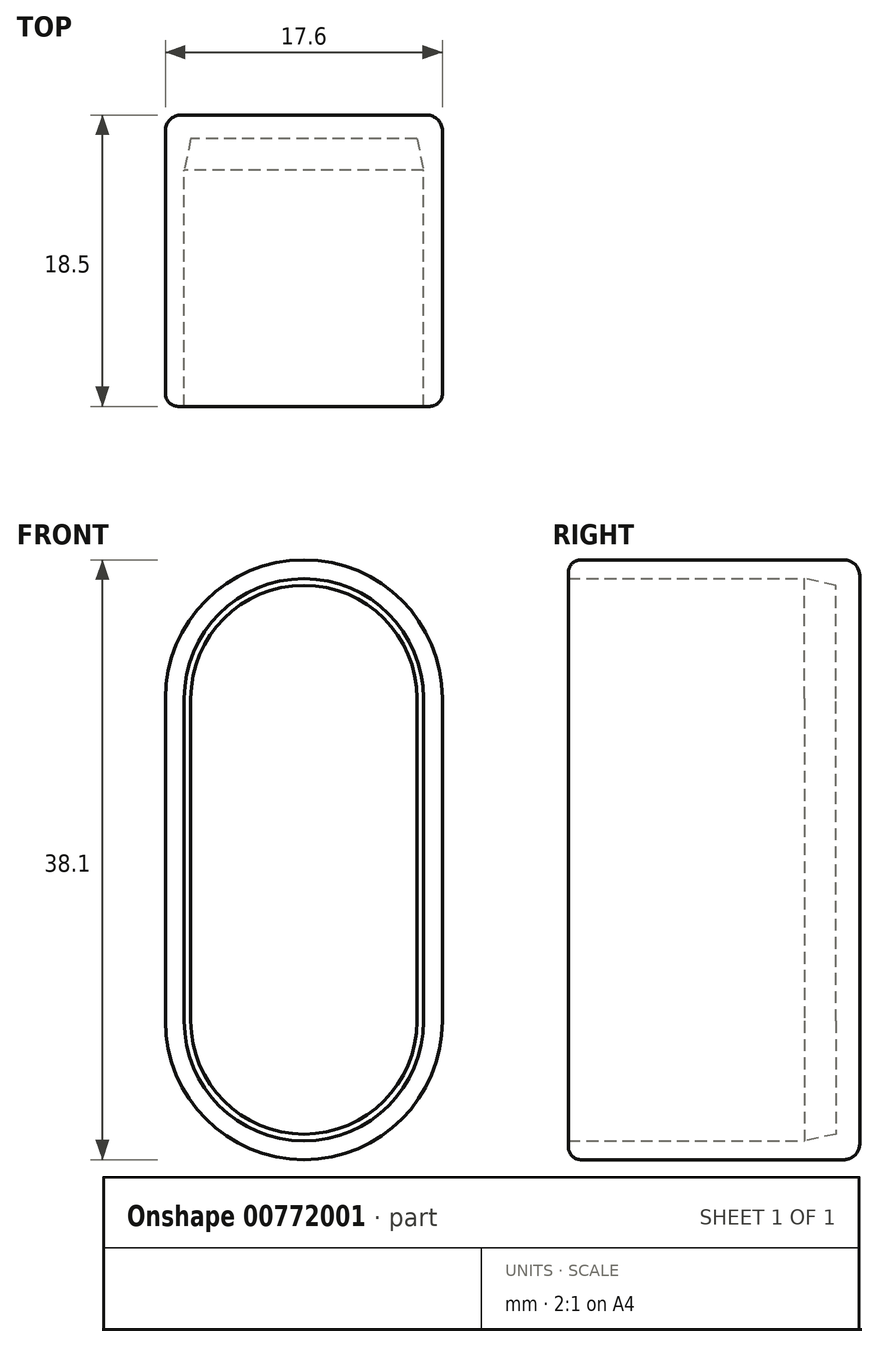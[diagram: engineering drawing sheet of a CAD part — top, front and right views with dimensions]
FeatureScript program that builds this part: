
annotation { "Feature Type Name" : "Feature", "Feature Type Description" : "" }
export const myFeature = defineFeature(function(context is Context, id is Id, definition is map)
    precondition{}
    {
        {
            var Q0;
            Q0=qCreatedBy(makeId("Front.planeOp"),FACE);
            var sketch = newSketch(context, id + "F0", { "sketchPlane" : qUnion([Q0])});
            skLineSegment(sketch, "E0", {"start": v(0, 0) * mm, "end": v(0, 20.5) * mm, "construction": true});
            skArc(sketch, "E1", {"start": v(7.6, 20.5) * mm, "mid": v(0, 28.1) * mm, "end": v(-7.6, 20.5) * mm});
            skArc(sketch, "E2", {"start": v(-7.6, 0) * mm, "mid": v(0, -7.6) * mm, "end": v(7.6, 0) * mm});
            skLineSegment(sketch, "E3", {"start": v(-7.6, 20.5) * mm, "end": v(-7.6, 0) * mm});
            skLineSegment(sketch, "E4", {"start": v(7.6, 20.5) * mm, "end": v(7.6, 0) * mm});
            skArc(sketch, "E5.0", {"start": v(8.8, 20.5) * mm, "mid": v(0, 29.3) * mm, "end": v(-8.8, 20.5) * mm});
            skLineSegment(sketch, "E5.1", {"start": v(8.8, 20.5) * mm, "end": v(8.8, 0) * mm});
            skArc(sketch, "E5.2", {"start": v(-8.8, 0) * mm, "mid": v(0, -8.8) * mm, "end": v(8.8, 0) * mm});
            skLineSegment(sketch, "E5.3", {"start": v(-8.8, 20.5) * mm, "end": v(-8.8, 0) * mm});
            skSolve(sketch);
        }
        {
            var Q0;
            Q0=makeQuery(id+"F0.imprint","IMPRINT",FACE,{"disambiguationData":[TD([[makeQuery(id+"F0.imprint","IMPRINT",EDGE,{"derivedFrom":sQuery(id+"F0.wireOp",EDGE,"E1")}),-1.0]])]});
            extrude(context, id + "F1", {"entities" : qUnion([Q0]), "depth" : 15 * mm, "offsetDistance" : 25 * mm});
        }
        {
            var Q0;
            Q0=makeQuery(id+"F1.opExtrude","CAP_FACE",FACE,{"disambiguationData":[OSD([sQuery(id+"F0.wireOp",EDGE,"E1"),sQuery(id+"F0.wireOp",EDGE,"E2"),sQuery(id+"F0.wireOp",EDGE,"E3"),sQuery(id+"F0.wireOp",EDGE,"E4"),sQuery(id+"F0.wireOp",EDGE,"E5.0"),sQuery(id+"F0.wireOp",EDGE,"E5.1"),sQuery(id+"F0.wireOp",EDGE,"E5.2"),sQuery(id+"F0.wireOp",EDGE,"E5.3")])],"isStart":true});
            cPlane(context, id + "F2", {"entities" : qUnion([Q0]), "cplaneType" : CPlaneType.OFFSET, "offset" : 2.4 * mm, "width" : 150 * mm, "height" : 150 * mm});
        }
        {
            var Q0;
            Q0=qCreatedBy(id+"F2.planeOp",FACE);
            var sketch = newSketch(context, id + "F3", { "sketchPlane" : qUnion([Q0])});
            skLineSegment(sketch, "E6.0", {"start": v(-7.1, 20.5) * mm, "end": v(-7.1, 0) * mm});
            skArc(sketch, "E6.1", {"start": v(-7.1, 20.5) * mm, "mid": v(0, 27.6) * mm, "end": v(7.1, 20.5) * mm});
            skLineSegment(sketch, "E6.2", {"start": v(7.1, 20.5) * mm, "end": v(7.1, 0) * mm});
            skArc(sketch, "E6.3", {"start": v(7.1, 0) * mm, "mid": v(0, -7.1) * mm, "end": v(-7.1, 0) * mm});
            skSolve(sketch);
        }
        {
            var Q0;
            Q0=makeQuery(id+"F1.opExtrude","CAP_FACE",FACE,{"disambiguationData":[OSD([sQuery(id+"F0.wireOp",EDGE,"E1"),sQuery(id+"F0.wireOp",EDGE,"E2"),sQuery(id+"F0.wireOp",EDGE,"E3"),sQuery(id+"F0.wireOp",EDGE,"E4"),sQuery(id+"F0.wireOp",EDGE,"E5.0"),sQuery(id+"F0.wireOp",EDGE,"E5.1"),sQuery(id+"F0.wireOp",EDGE,"E5.2"),sQuery(id+"F0.wireOp",EDGE,"E5.3")])],"isStart":true});
            var sketch = newSketch(context, id + "F4", { "sketchPlane" : qUnion([Q0])});
            skLineSegment(sketch, "E7.0", {"start": v(-8.8, 20.5) * mm, "end": v(-8.8, 0) * mm});
            skArc(sketch, "E8.0", {"start": v(8.8, 0) * mm, "mid": v(0, -8.8) * mm, "end": v(-8.8, 0) * mm});
            skLineSegment(sketch, "E9.0", {"start": v(8.8, 20.5) * mm, "end": v(8.8, 0) * mm});
            skArc(sketch, "E10.0", {"start": v(-8.8, 20.5) * mm, "mid": v(0, 29.3) * mm, "end": v(8.8, 20.5) * mm});
            skSolve(sketch);
        }
        {
            var Q0;
            Q0 = qSketchRegion(id + "F4", true);
            extrude(context, id + "F5", {"entities" : qUnion([Q0]), "operationType" : NewBodyOperationType.ADD, "depth" : 2 * mm, "offsetDistance" : 25 * mm});
        }
        {
            var Q0;
            Q0=makeQuery(id+"F5.opExtrude","CAP_FACE",FACE,{"disambiguationData":[OSD([sQuery(id+"F4.wireOp",EDGE,"E7.0"),sQuery(id+"F4.wireOp",EDGE,"E8.0"),sQuery(id+"F4.wireOp",EDGE,"E9.0"),sQuery(id+"F4.wireOp",EDGE,"E10.0")])],"isStart":false});
            cPlane(context, id + "F6", {"entities" : qUnion([Q0]), "cplaneType" : CPlaneType.OFFSET, "offset" : 2 * mm, "oppositeDirection" : true, "width" : 150 * mm, "height" : 150 * mm});
        }
        {
            var Q0;
            Q0=qCreatedBy(id+"F6.planeOp",FACE);
            var sketch = newSketch(context, id + "F7", { "sketchPlane" : qUnion([Q0])});
            skLineSegment(sketch, "E11.0", {"start": v(7.6, 20.5) * mm, "end": v(7.6, 0) * mm});
            skArc(sketch, "E12.0", {"start": v(7.6, 0) * mm, "mid": v(0, -7.6) * mm, "end": v(-7.6, 0) * mm});
            skLineSegment(sketch, "E13.0", {"start": v(-7.6, 20.5) * mm, "end": v(-7.6, 0) * mm});
            skArc(sketch, "E14.0", {"start": v(-7.6, 20.5) * mm, "mid": v(0, 28.1) * mm, "end": v(7.6, 20.5) * mm});
            skSolve(sketch);
        }
        {
            var Q1;
            Q1 = qSketchRegion(id + "F3", true);
            var Q2;
            Q2 = qSketchRegion(id + "F7", true);
            loft(context, id + "F8", {"operationType" : NewBodyOperationType.REMOVE, "sheetProfilesArray" : [{ "sheetProfileEntities" : qUnion([Q1]) }, { "sheetProfileEntities" : qUnion([Q2]) }]});
        }
        {
            var Q0;
            Q0=makeQuery(id+"F5.opExtrude","CAP_FACE",FACE,{"disambiguationData":[OSD([sQuery(id+"F4.wireOp",EDGE,"E7.0"),sQuery(id+"F4.wireOp",EDGE,"E8.0"),sQuery(id+"F4.wireOp",EDGE,"E9.0"),sQuery(id+"F4.wireOp",EDGE,"E10.0")])],"isStart":false});
            var sketch = newSketch(context, id + "F9", { "sketchPlane" : qUnion([Q0])});
            skLineSegment(sketch, "E15.0", {"start": v(-8.8, 20.5) * mm, "end": v(-8.8, 0) * mm});
            skArc(sketch, "E16.0", {"start": v(-8.8, 20.5) * mm, "mid": v(0, 29.3) * mm, "end": v(8.8, 20.5) * mm});
            skLineSegment(sketch, "E17.0", {"start": v(8.8, 20.5) * mm, "end": v(8.8, 0) * mm});
            skArc(sketch, "E18.0", {"start": v(8.8, 0) * mm, "mid": v(0, -8.8) * mm, "end": v(-8.8, 0) * mm});
            skSolve(sketch);
        }
        {
            var Q0;
            Q0 = qSketchRegion(id + "F9", true);
            extrude(context, id + "F10", {"entities" : qUnion([Q0]), "operationType" : NewBodyOperationType.ADD, "depth" : 1.5 * mm, "offsetDistance" : 25 * mm});
        }
        {
            var Q0;
            Q0=makeQuery(id+"F10.opExtrude","CAP_EDGE",EDGE,{"disambiguationData":[OSD([sQuery(id+"F9.wireOp",EDGE,"E18.0")])],"isStart":false});
            fillet(context, id + "F11", {"entities" : qUnion([Q0]), "radius" : 1 * mm, "tangentPropagation" : true, "allowEdgeOverflow" : false});
        }
        {
            var Q0;
            Q0=makeQuery(id+"F1.opExtrude","CAP_EDGE",EDGE,{"disambiguationData":[OSD([sQuery(id+"F0.wireOp",EDGE,"E5.1")])],"isStart":false});
            fillet(context, id + "F12", {"entities" : qUnion([Q0]), "radius" : 0.8 * mm, "tangentPropagation" : true, "allowEdgeOverflow" : false});
        }
    });
